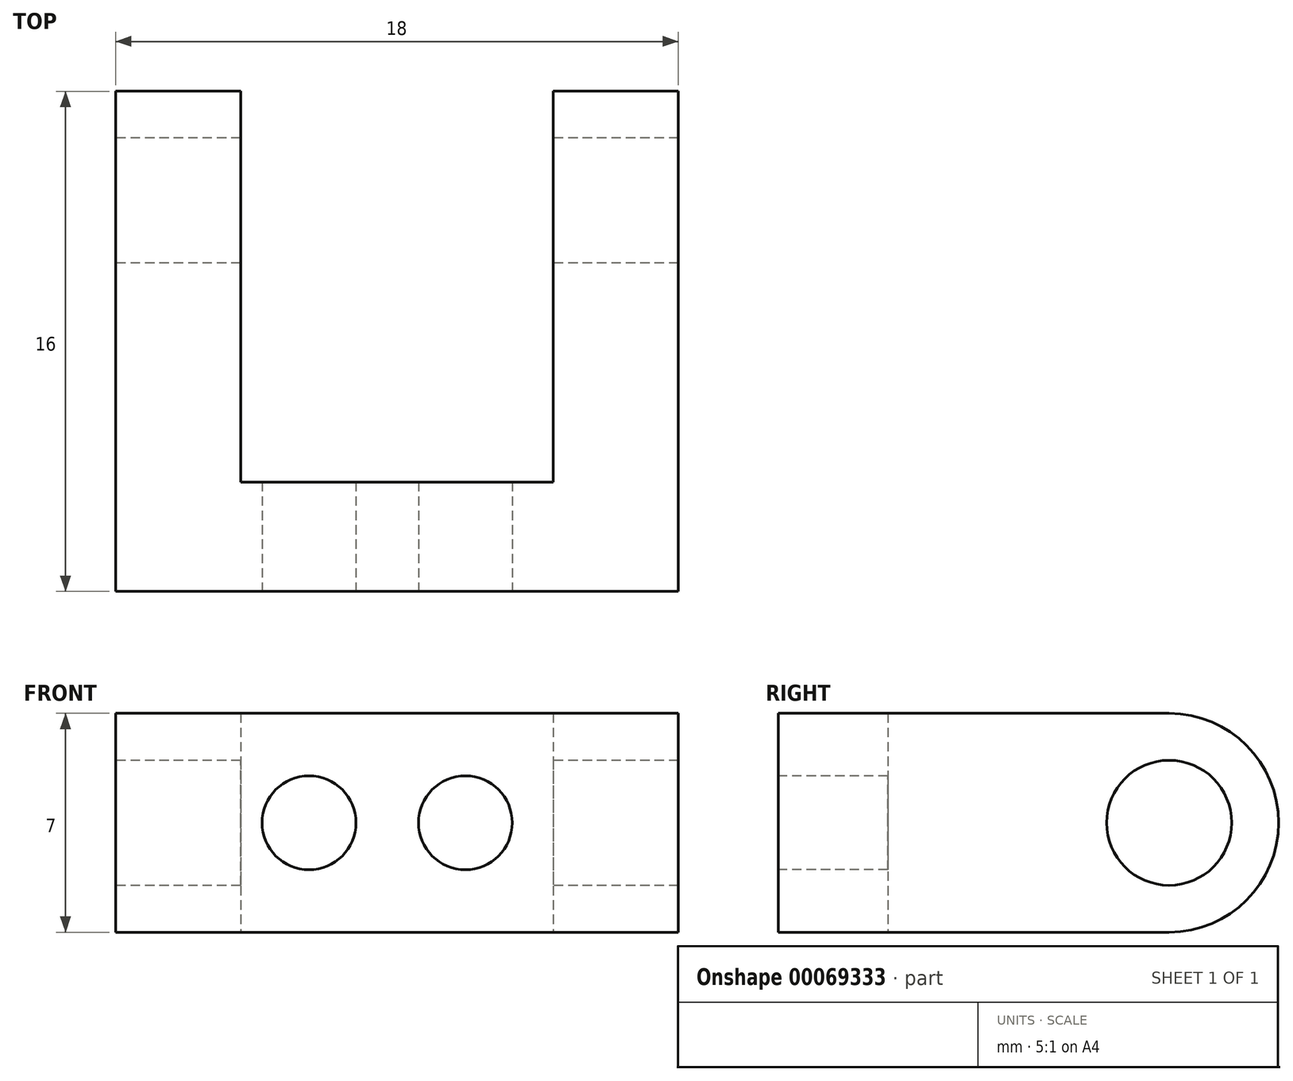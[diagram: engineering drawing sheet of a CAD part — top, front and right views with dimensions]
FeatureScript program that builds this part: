
annotation { "Feature Type Name" : "Feature", "Feature Type Description" : "" }
export const myFeature = defineFeature(function(context is Context, id is Id, definition is map)
    precondition{}
    {
        {
            var Q0;
            Q0=qCreatedBy(makeId("Top.planeOp"),FACE);
            var sketch = newSketch(context, id + "F0", { "sketchPlane" : qUnion([Q0])});
            skLineSegment(sketch, "E0", {"start": v(0.31, 25.5) * mm, "end": v(0.31, -22.93) * mm, "construction": true});
            skLineSegment(sketch, "E1", {"start": v(-18.5, -3.32) * mm, "end": v(28.23, -3.32) * mm, "construction": true});
            skLineSegment(sketch, "E2.0", {"start": v(-8.69, 25.5) * mm, "end": v(-8.69, -22.93) * mm, "construction": true});
            skLineSegment(sketch, "E3.0", {"start": v(-4.69, 25.5) * mm, "end": v(-4.69, -22.93) * mm, "construction": true});
            skLineSegment(sketch, "E4.0", {"start": v(-18.5, 0.18) * mm, "end": v(28.23, 0.18) * mm, "construction": true});
            skLineSegment(sketch, "E5.0", {"start": v(-18.5, 9.18) * mm, "end": v(28.23, 9.18) * mm, "construction": true});
            skLineSegment(sketch, "E6.0", {"start": v(-5.69, 25.5) * mm, "end": v(-5.69, -22.93) * mm, "construction": true});
            skLineSegment(sketch, "E7", {"start": v(0.31, -3.32) * mm, "end": v(-8.69, -3.32) * mm});
            skLineSegment(sketch, "E8", {"start": v(-8.69, -3.32) * mm, "end": v(-8.69, 0.18) * mm});
            skLineSegment(sketch, "E9", {"start": v(-5.69, 0.18) * mm, "end": v(-4.69, 0.18) * mm});
            skLineSegment(sketch, "E10", {"start": v(-4.69, 0.18) * mm, "end": v(-4.69, 9.18) * mm});
            skLineSegment(sketch, "E11", {"start": v(-4.69, 9.18) * mm, "end": v(0.31, 9.18) * mm});
            skLineSegment(sketch, "E12.MirrorCS", {"start": v(5.31, 9.18) * mm, "end": v(0.31, 9.18) * mm});
            skLineSegment(sketch, "E13.MirrorCS", {"start": v(5.31, 0.18) * mm, "end": v(5.31, 9.18) * mm});
            skLineSegment(sketch, "E14.MirrorCS", {"start": v(9.31, -3.32) * mm, "end": v(9.31, 0.18) * mm});
            skLineSegment(sketch, "E15.MirrorCS", {"start": v(0.31, -3.32) * mm, "end": v(9.31, -3.32) * mm});
            skLineSegment(sketch, "E16", {"start": v(-4.69, 9.18) * mm, "end": v(-8.69, 9.18) * mm});
            skLineSegment(sketch, "E17", {"start": v(-8.69, 9.18) * mm, "end": v(-8.69, 0.18) * mm});
            skLineSegment(sketch, "E18", {"start": v(5.31, 9.18) * mm, "end": v(9.31, 9.18) * mm});
            skLineSegment(sketch, "E19", {"start": v(9.31, 9.18) * mm, "end": v(9.31, 0.18) * mm});
            skPoint(sketch, "E20.MirrorCS.end.orphan", {"position": v(5.31, 0.18) * mm});
            skLineSegment(sketch, "E21", {"start": v(-4.69, 0.18) * mm, "end": v(5.31, 0.18) * mm});
            skSolve(sketch);
        }
        {
            var Q0;
            Q0=makeQuery(id+"F0.imprint","IMPRINT",FACE,{"disambiguationData":[TD([[makeQuery(id+"F0.imprint","IMPRINT",EDGE,{"derivedFrom":sQuery(id+"F0.wireOp",EDGE,"E7")}),-1.0]])]});
            extrude(context, id + "F1", {"entities" : qUnion([Q0]), "depth" : 7 * mm});
        }
        {
            var Q0;
            Q0=makeQuery(id+"F1.opExtrude","SWEPT_FACE",FACE,{"disambiguationData":[OSD([sQuery(id+"F0.wireOp",EDGE,"E8"),sQuery(id+"F0.wireOp",EDGE,"E17")])]});
            var sketch = newSketch(context, id + "F2", { "sketchPlane" : qUnion([Q0])});
            skLineSegment(sketch, "E22.0.0", {"start": v(-9.18, 0) * mm, "end": v(3.32, 0) * mm});
            skLineSegment(sketch, "E22.0.1", {"start": v(3.32, 0) * mm, "end": v(3.32, 7) * mm});
            skLineSegment(sketch, "E22.0.2", {"start": v(3.32, 7) * mm, "end": v(-9.18, 7) * mm});
            skLineSegment(sketch, "E22.0.3", {"start": v(-9.18, 7) * mm, "end": v(-9.18, 0) * mm});
            skCircle(sketch, "E23", {"center": v(-9.18, 3.5) * mm, "radius": 2 * mm});
            skCircle(sketch, "E24", {"center": v(-9.18, 3.5) * mm, "radius": 3.5 * mm});
            skSolve(sketch);
        }
        {
            var Q0;
            {var subQ0=sQuery(id+"F2.wireOp",EDGE,"E23");var subQ1=sQuery(id+"F2.wireOp",EDGE,"E22.0.3");var subQ2=makeQuery(id+"F2.imprint","INTERSECT",VERTEX,{"disambiguationData":[OD(0.0)],"derivedFrom":[subQ1,subQ0]});Q0=makeQuery(id+"F2.imprint","IMPRINT",FACE,{"disambiguationData":[TD([[makeQuery(id+"F2.imprint","IMPRINT",EDGE,{"disambiguationData":[TD([[subQ2,-1.0]])],"derivedFrom":subQ1}),1.0]])]});}
            var Q1;
            Q1=makeQuery(id+"F1.opExtrude","SWEPT_FACE",FACE,{"disambiguationData":[OSD([sQuery(id+"F0.wireOp",EDGE,"E14.MirrorCS"),sQuery(id+"F0.wireOp",EDGE,"E19")])]});
            extrude(context, id + "F3", {"entities" : qUnion([Q0]), "operationType" : NewBodyOperationType.REMOVE, "endBound" : BoundingType.UP_TO_SURFACE, "oppositeDirection" : true, "endBoundEntityFace" : qUnion([Q1]), "depth" : 25 * mm});
        }
        {
            var Q0;
            {var subQ1=sQuery(id+"F2.wireOp",EDGE,"E22.0.3");var subQ3=sQuery(id+"F2.wireOp",EDGE,"E23");var subQ4=makeQuery(id+"F2.imprint","INTERSECT",VERTEX,{"disambiguationData":[OD(0.0)],"derivedFrom":[subQ1,subQ3]});Q0=makeQuery(id+"F2.imprint","IMPRINT",FACE,{"disambiguationData":[TD([[makeQuery(id+"F2.imprint","IMPRINT",EDGE,{"disambiguationData":[TD([[subQ4,-1.0]])],"derivedFrom":subQ3}),-1.0]])]});}
            var Q1;
            Q1=makeQuery(id+"F1.opExtrude","SWEPT_FACE",FACE,{"disambiguationData":[OSD([sQuery(id+"F0.wireOp",EDGE,"E10")])]});
            extrude(context, id + "F4", {"entities" : qUnion([Q0]), "operationType" : NewBodyOperationType.ADD, "endBound" : BoundingType.UP_TO_SURFACE, "oppositeDirection" : true, "endBoundEntityFace" : qUnion([Q1]), "depth" : 25 * mm});
        }
        {
            var Q0;
            Q0=makeQuery(id+"F1.opExtrude","SWEPT_FACE",FACE,{"disambiguationData":[OSD([sQuery(id+"F0.wireOp",EDGE,"E14.MirrorCS"),sQuery(id+"F0.wireOp",EDGE,"E19")])]});
            var sketch = newSketch(context, id + "F5", { "sketchPlane" : qUnion([Q0])});
            skArc(sketch, "E25.0.0", {"start": v(9.18, 5.5) * mm, "mid": v(7.18, 3.5) * mm, "end": v(9.18, 1.5) * mm});
            skLineSegment(sketch, "E25.0.1", {"start": v(9.18, 5.5) * mm, "end": v(9.18, 7) * mm});
            skLineSegment(sketch, "E25.0.2", {"start": v(9.18, 7) * mm, "end": v(-3.32, 7) * mm});
            skLineSegment(sketch, "E25.0.3", {"start": v(-3.32, 7) * mm, "end": v(-3.32, 0) * mm});
            skLineSegment(sketch, "E25.0.4", {"start": v(-3.32, 0) * mm, "end": v(9.18, 0) * mm});
            skLineSegment(sketch, "E25.0.5", {"start": v(9.18, 0) * mm, "end": v(9.18, 1.5) * mm});
            skCircle(sketch, "E26", {"center": v(9.18, 3.5) * mm, "radius": 3.5 * mm});
            skCircle(sketch, "E27", {"center": v(9.18, 3.5) * mm, "radius": 2 * mm});
            skSolve(sketch);
        }
        {
            var Q0;
            Q0 = qSketchRegion(id + "F5", true);
            var Q1;
            Q1=makeQuery(id+"F1.opExtrude","SWEPT_FACE",FACE,{"disambiguationData":[OSD([sQuery(id+"F0.wireOp",EDGE,"E13.MirrorCS")])]});
            extrude(context, id + "F6", {"entities" : qUnion([Q0]), "operationType" : NewBodyOperationType.ADD, "endBound" : BoundingType.UP_TO_SURFACE, "oppositeDirection" : true, "endBoundEntityFace" : qUnion([Q1]), "depth" : 25 * mm});
        }
        {
            var Q0;
            Q0=makeQuery(id+"F1.opExtrude","SWEPT_FACE",FACE,{"disambiguationData":[OSD([sQuery(id+"F0.wireOp",EDGE,"E7"),sQuery(id+"F0.wireOp",EDGE,"E15.MirrorCS")])]});
            var sketch = newSketch(context, id + "F7", { "sketchPlane" : qUnion([Q0])});
            skLineSegment(sketch, "E28.0.0", {"start": v(-8.69, 7) * mm, "end": v(-8.69, 0) * mm});
            skLineSegment(sketch, "E28.0.1", {"start": v(-8.69, 0) * mm, "end": v(9.31, 0) * mm});
            skLineSegment(sketch, "E28.0.2", {"start": v(9.31, 0) * mm, "end": v(9.31, 7) * mm});
            skLineSegment(sketch, "E28.0.3", {"start": v(9.31, 7) * mm, "end": v(-8.69, 7) * mm});
            skLineSegment(sketch, "E29", {"start": v(0, 8.73) * mm, "end": v(0, -1.44) * mm, "construction": true});
            skLineSegment(sketch, "E30.0", {"start": v(-2.5, 7) * mm, "end": v(-2.5, 0) * mm, "construction": true});
            skLineSegment(sketch, "E31.0", {"start": v(2.5, 7) * mm, "end": v(2.5, 0) * mm, "construction": true});
            skCircle(sketch, "E32", {"center": v(-2.5, 3.5) * mm, "radius": 1.5 * mm});
            skCircle(sketch, "E33", {"center": v(2.5, 3.5) * mm, "radius": 1.5 * mm});
            skSolve(sketch);
        }
        {
            var Q0;
            Q0=makeQuery(id+"F7.imprint","IMPRINT",FACE,{"disambiguationData":[TD([[makeQuery(id+"F7.imprint","IMPRINT",EDGE,{"derivedFrom":sQuery(id+"F7.wireOp",EDGE,"E32")}),1.0]])]});
            var Q1;
            Q1=makeQuery(id+"F7.imprint","IMPRINT",FACE,{"disambiguationData":[TD([[makeQuery(id+"F7.imprint","IMPRINT",EDGE,{"derivedFrom":sQuery(id+"F7.wireOp",EDGE,"E33")}),1.0]])]});
            var Q2;
            Q2=makeQuery(id+"F1.opExtrude","SWEPT_FACE",FACE,{"disambiguationData":[OSD([sQuery(id+"F0.wireOp",EDGE,"E21")])]});
            extrude(context, id + "F8", {"entities" : qUnion([Q0, Q1]), "operationType" : NewBodyOperationType.REMOVE, "endBound" : BoundingType.UP_TO_SURFACE, "oppositeDirection" : true, "endBoundEntityFace" : qUnion([Q2]), "depth" : 25 * mm});
        }
    });
